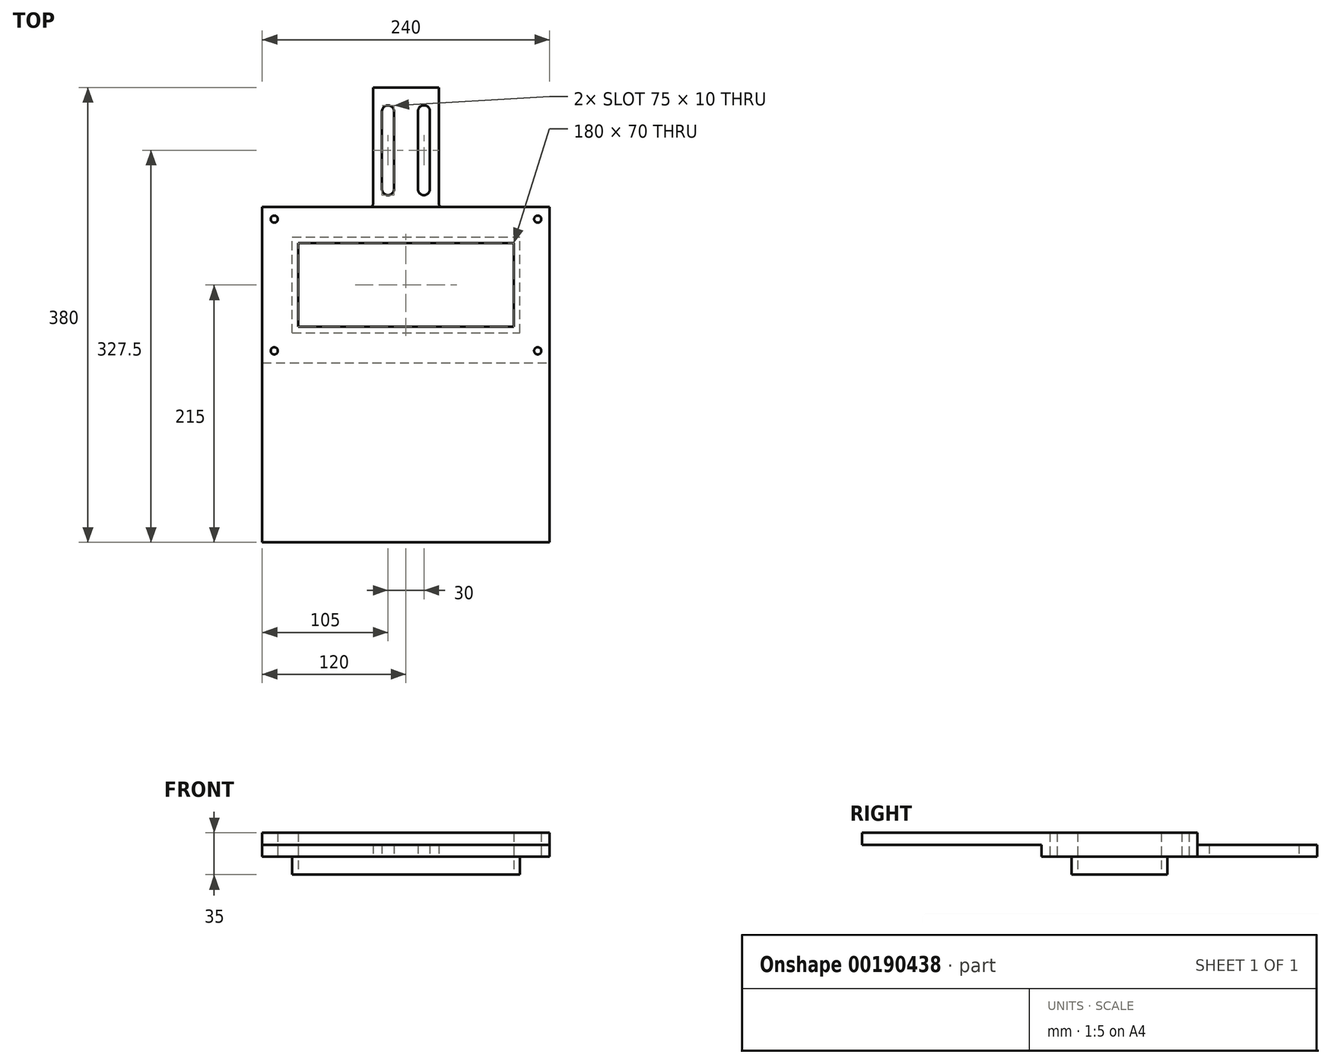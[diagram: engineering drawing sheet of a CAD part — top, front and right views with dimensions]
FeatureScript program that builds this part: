
annotation { "Feature Type Name" : "Feature", "Feature Type Description" : "" }
export const myFeature = defineFeature(function(context is Context, id is Id, definition is map)
    precondition{}
    {
        {
            var Q0;
            Q0=qCreatedBy(makeId("Top.planeOp"),FACE);
            var sketch = newSketch(context, id + "F0", { "sketchPlane" : qUnion([Q0])});
            skLineSegment(sketch, "E0.bottom", {"start": v(0, 0) * mm, "end": v(600, 0) * mm, "construction": true});
            skLineSegment(sketch, "E0.top", {"start": v(0, 500) * mm, "end": v(600, 500) * mm, "construction": true});
            skLineSegment(sketch, "E0.left", {"start": v(0, 0) * mm, "end": v(0, 500) * mm, "construction": true});
            skLineSegment(sketch, "E0.right", {"start": v(600, 0) * mm, "end": v(600, 500) * mm, "construction": true});
            skLineSegment(sketch, "E1.bottom", {"start": v(200, 200) * mm, "end": v(440, 200) * mm, "construction": true});
            skLineSegment(sketch, "E1.top", {"start": v(200, 330) * mm, "end": v(440, 330) * mm, "construction": true});
            skLineSegment(sketch, "E1.left", {"start": v(200, 200) * mm, "end": v(200, 330) * mm, "construction": true});
            skLineSegment(sketch, "E1.right", {"start": v(440, 200) * mm, "end": v(440, 330) * mm, "construction": true});
            skSolve(sketch);
        }
        {
            var Q0;
            Q0=qCreatedBy(makeId("Top.planeOp"),FACE);
            var sketch = newSketch(context, id + "F1", { "sketchPlane" : qUnion([Q0])});
            skLineSegment(sketch, "E2.top", {"start": v(200, 200) * mm, "end": v(440, 200) * mm});
            skLineSegment(sketch, "E2.left", {"start": v(200, 330) * mm, "end": v(200, 200) * mm});
            skLineSegment(sketch, "E2.right", {"start": v(440, 330) * mm, "end": v(440, 200) * mm});
            skLineSegment(sketch, "E3.top", {"start": v(292.5, 430) * mm, "end": v(347.5, 430) * mm});
            skLineSegment(sketch, "E3.left", {"start": v(292.5, 333) * mm, "end": v(292.5, 430) * mm});
            skLineSegment(sketch, "E3.right", {"start": v(347.5, 333) * mm, "end": v(347.5, 430) * mm});
            skPoint(sketch, "E4", {"position": v(320, 330) * mm});
            skLineSegment(sketch, "E5", {"start": v(320, 345) * mm, "end": v(320, 410) * mm, "construction": true});
            skLineSegment(sketch, "E6", {"start": v(305, 410) * mm, "end": v(305, 345) * mm, "construction": true});
            skLineSegment(sketch, "E7.MirrorCS", {"start": v(335, 410) * mm, "end": v(335, 345) * mm, "construction": true});
            skArc(sketch, "E8.0.startCap", {"start": v(300, 410) * mm, "mid": v(305, 415) * mm, "end": v(310, 410) * mm});
            skArc(sketch, "E8.0.endCap", {"start": v(310, 345) * mm, "mid": v(305, 340) * mm, "end": v(300, 345) * mm});
            skLineSegment(sketch, "E8.0.left", {"start": v(310, 410) * mm, "end": v(310, 345) * mm});
            skLineSegment(sketch, "E8.0.right", {"start": v(300, 410) * mm, "end": v(300, 345) * mm});
            skArc(sketch, "E8.2.startCap", {"start": v(330, 410) * mm, "mid": v(335, 415) * mm, "end": v(340, 410) * mm});
            skArc(sketch, "E8.2.endCap", {"start": v(340, 345) * mm, "mid": v(335, 340) * mm, "end": v(330, 345) * mm});
            skLineSegment(sketch, "E8.2.left", {"start": v(340, 410) * mm, "end": v(340, 345) * mm});
            skLineSegment(sketch, "E8.2.right", {"start": v(330, 410) * mm, "end": v(330, 345) * mm});
            skLineSegment(sketch, "E9", {"start": v(289.5, 330) * mm, "end": v(200, 330) * mm});
            skLineSegment(sketch, "E10", {"start": v(350.5, 330) * mm, "end": v(440, 330) * mm});
            skPoint(sketch, "E11.visualSharp", {"position": v(292.5, 330) * mm});
            skArc(sketch, "E11.filletArc", {"start": v(289.5, 330) * mm, "mid": v(291.62, 330.88) * mm, "end": v(292.5, 333) * mm});
            skPoint(sketch, "E12.visualSharp", {"position": v(347.5, 330) * mm});
            skArc(sketch, "E12.filletArc", {"start": v(347.5, 333) * mm, "mid": v(348.38, 330.88) * mm, "end": v(350.5, 330) * mm});
            skPoint(sketch, "E13", {"position": v(320, 430) * mm});
            skPoint(sketch, "E14", {"position": v(320, 200) * mm});
            skLineSegment(sketch, "E15.bottom", {"start": v(410, 300) * mm, "end": v(230, 300) * mm});
            skLineSegment(sketch, "E15.top", {"start": v(410, 230) * mm, "end": v(230, 230) * mm});
            skLineSegment(sketch, "E15.left", {"start": v(410, 300) * mm, "end": v(410, 230) * mm});
            skLineSegment(sketch, "E15.right", {"start": v(230, 300) * mm, "end": v(230, 230) * mm});
            skPoint(sketch, "E15.middle", {"position": v(320, 265) * mm});
            skPoint(sketch, "E15.middle.positionSnap0", {"position": v(200, 265) * mm});
            skPoint(sketch, "E15.centerSnap0", {"position": v(200, 265) * mm});
            skLineSegment(sketch, "E16.0", {"start": v(415, 305) * mm, "end": v(225, 305) * mm});
            skLineSegment(sketch, "E16.1", {"start": v(415, 305) * mm, "end": v(415, 225) * mm});
            skLineSegment(sketch, "E16.2", {"start": v(415, 225) * mm, "end": v(225, 225) * mm});
            skLineSegment(sketch, "E16.3", {"start": v(225, 305) * mm, "end": v(225, 225) * mm});
            skLineSegment(sketch, "E17.bottom", {"start": v(200, 330) * mm, "end": v(210, 330) * mm, "construction": true});
            skLineSegment(sketch, "E17.top", {"start": v(200, 320) * mm, "end": v(210, 320) * mm, "construction": true});
            skLineSegment(sketch, "E17.left", {"start": v(200, 330) * mm, "end": v(200, 320) * mm, "construction": true});
            skLineSegment(sketch, "E17.right", {"start": v(210, 330) * mm, "end": v(210, 320) * mm, "construction": true});
            skLineSegment(sketch, "E18.bottom", {"start": v(440, 200) * mm, "end": v(430, 200) * mm, "construction": true});
            skLineSegment(sketch, "E18.top", {"start": v(440, 210) * mm, "end": v(430, 210) * mm, "construction": true});
            skLineSegment(sketch, "E18.left", {"start": v(440, 200) * mm, "end": v(440, 210) * mm, "construction": true});
            skLineSegment(sketch, "E18.right", {"start": v(430, 200) * mm, "end": v(430, 210) * mm, "construction": true});
            skCircle(sketch, "E19", {"center": v(430, 210) * mm, "radius": 3 * mm});
            skCircle(sketch, "E20", {"center": v(210, 320) * mm, "radius": 3 * mm});
            skCircle(sketch, "E21", {"center": v(430, 320) * mm, "radius": 3 * mm});
            skCircle(sketch, "E22", {"center": v(210, 210) * mm, "radius": 3 * mm});
            skLineSegment(sketch, "E23", {"start": v(289.5, 330) * mm, "end": v(350.5, 330) * mm});
            skLineSegment(sketch, "E24.top", {"start": v(200, 50) * mm, "end": v(440, 50) * mm});
            skLineSegment(sketch, "E24.left", {"start": v(200, 200) * mm, "end": v(200, 50) * mm});
            skLineSegment(sketch, "E24.right", {"start": v(440, 200) * mm, "end": v(440, 50) * mm});
            skSolve(sketch);
        }
        {
            var Q0;
            Q0=makeQuery(id+"F1.imprint","IMPRINT",FACE,{"disambiguationData":[TD([[makeQuery(id+"F1.imprint","IMPRINT",EDGE,{"derivedFrom":sQuery(id+"F1.wireOp",EDGE,"E3.top")}),-1.0]])]});
            var Q1;
            Q1=makeQuery(id+"F1.imprint","IMPRINT",FACE,{"disambiguationData":[TD([[makeQuery(id+"F1.imprint","IMPRINT",EDGE,{"derivedFrom":sQuery(id+"F1.wireOp",EDGE,"E2.left")}),1.0]])]});
            extrude(context, id + "F2", {"entities" : qUnion([Q0, Q1]), "depth" : 10 * mm});
        }
        {
            var Q0;
            Q0=makeQuery(id+"F1.imprint","IMPRINT",FACE,{"disambiguationData":[TD([[makeQuery(id+"F1.imprint","IMPRINT",EDGE,{"derivedFrom":sQuery(id+"F1.wireOp",EDGE,"E3.top")}),-1.0]])]});
            var Q1;
            Q1=makeQuery(id+"F1.imprint","IMPRINT",FACE,{"disambiguationData":[TD([[makeQuery(id+"F1.imprint","IMPRINT",EDGE,{"derivedFrom":sQuery(id+"F1.wireOp",EDGE,"E2.left")}),1.0]])]});
            var Q2;
            Q2=makeQuery(id+"F1.imprint","IMPRINT",FACE,{"disambiguationData":[TD([[makeQuery(id+"F1.imprint","IMPRINT",EDGE,{"derivedFrom":sQuery(id+"F1.wireOp",EDGE,"E15.bottom")}),-1.0]])]});
            extrude(context, id + "F3", {"entities" : qUnion([Q0, Q1, Q2]), "operationType" : NewBodyOperationType.ADD, "depth" : 5 * mm});
        }
        {
            var Q0;
            Q0=makeQuery(id+"F1.imprint","IMPRINT",FACE,{"disambiguationData":[TD([[makeQuery(id+"F1.imprint","IMPRINT",EDGE,{"derivedFrom":sQuery(id+"F1.wireOp",EDGE,"E2.left")}),1.0]])]});
            var Q1;
            Q1=makeQuery(id+"F1.imprint","IMPRINT",FACE,{"disambiguationData":[TD([[makeQuery(id+"F1.imprint","IMPRINT",EDGE,{"derivedFrom":sQuery(id+"F1.wireOp",EDGE,"E2.top")}),-1.0]])]});
            extrude(context, id + "F4", {"entities" : qUnion([Q0, Q1]), "depth" : 20 * mm, "hasSecondDirection" : true, "secondDirectionOppositeDirection" : false, "secondDirectionDepth" : 10 * mm});
        }
        {
            var Q0;
            Q0=makeQuery(id+"F1.imprint","IMPRINT",FACE,{"disambiguationData":[TD([[makeQuery(id+"F1.imprint","IMPRINT",EDGE,{"derivedFrom":sQuery(id+"F1.wireOp",EDGE,"E15.bottom")}),-1.0]])]});
            extrude(context, id + "F5", {"entities" : qUnion([Q0]), "operationType" : NewBodyOperationType.ADD, "depth" : 20 * mm, "hasSecondDirection" : true, "secondDirectionOppositeDirection" : true, "secondDirectionDepth" : 15 * mm});
        }
    });
